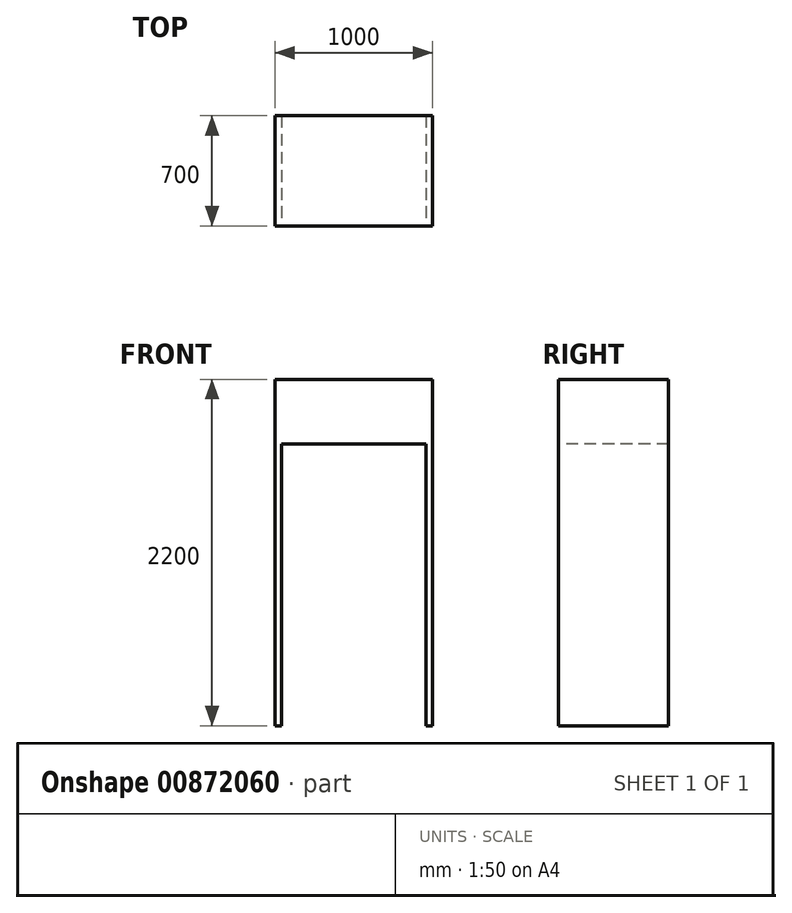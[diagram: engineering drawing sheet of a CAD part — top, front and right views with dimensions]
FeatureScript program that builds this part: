
annotation { "Feature Type Name" : "Feature", "Feature Type Description" : "" }
export const myFeature = defineFeature(function(context is Context, id is Id, definition is map)
    precondition{}
    {
        {
            var Q0;
            Q0=qCreatedBy(makeId("Top.planeOp"),FACE);
            var sketch = newSketch(context, id + "F0", { "sketchPlane" : qUnion([Q0])});
            skLineSegment(sketch, "E0.bottom", {"start": v(0, 0) * mm, "end": v(1000, 0) * mm});
            skLineSegment(sketch, "E0.top", {"start": v(0, 700) * mm, "end": v(1000, 700) * mm});
            skLineSegment(sketch, "E0.left", {"start": v(0, 0) * mm, "end": v(0, 700) * mm});
            skLineSegment(sketch, "E0.right", {"start": v(1000, 0) * mm, "end": v(1000, 700) * mm});
            skSolve(sketch);
        }
        {
            var Q0;
            Q0=qSketchRegion(id+"F0",true);
            extrude(context, id + "F1", {"entities" : qUnion([Q0]), "depth" : 2200 * mm, "offsetDistance" : 25 * mm});
        }
        {
            var Q0;
            Q0=makeQuery(id+"F1.opExtrude","SWEPT_FACE",FACE,{"disambiguationData":[OSD([sQuery(id+"F0.wireOp",EDGE,"E0.bottom")])]});
            var sketch = newSketch(context, id + "F2", { "sketchPlane" : qUnion([Q0])});
            skLineSegment(sketch, "E1.bottom", {"start": v(40, 0) * mm, "end": v(960, 0) * mm});
            skLineSegment(sketch, "E1.top", {"start": v(40, 1790) * mm, "end": v(960, 1790) * mm});
            skLineSegment(sketch, "E1.left", {"start": v(40, 0) * mm, "end": v(40, 1790) * mm});
            skLineSegment(sketch, "E1.right", {"start": v(960, 0) * mm, "end": v(960, 1790) * mm});
            skSolve(sketch);
        }
        {
            var Q0;
            Q0=qSketchRegion(id+"F2",true);
            extrude(context, id + "F3", {"entities" : qUnion([Q0]), "operationType" : NewBodyOperationType.REMOVE, "endBound" : BoundingType.THROUGH_ALL, "oppositeDirection" : true, "depth" : 25 * mm, "offsetDistance" : 25 * mm});
        }
    });
